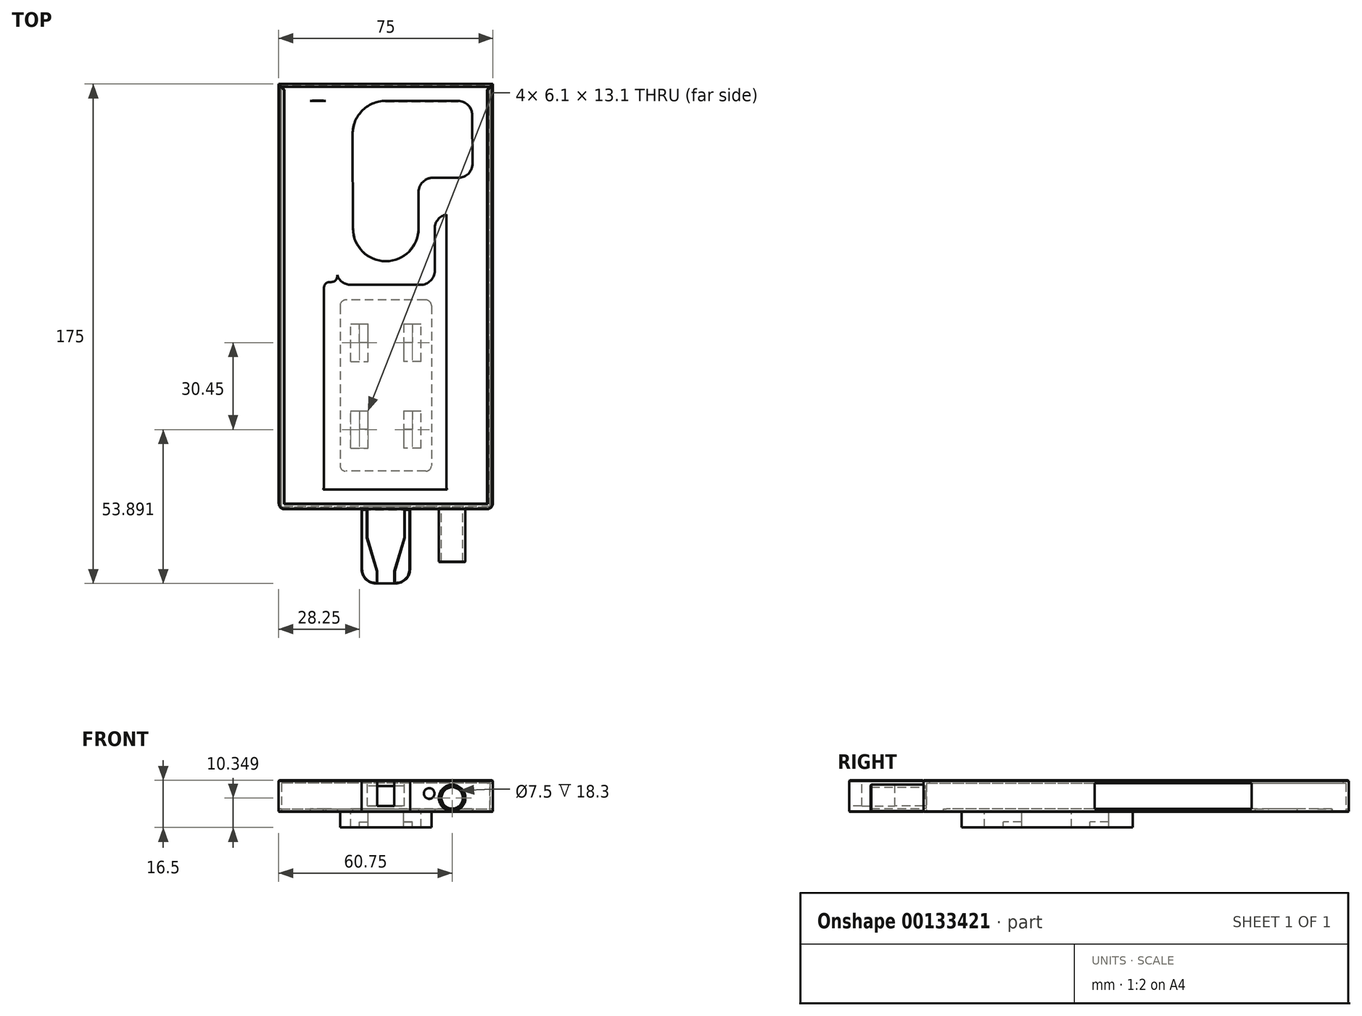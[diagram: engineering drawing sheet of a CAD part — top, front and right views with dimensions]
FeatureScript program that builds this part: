
annotation { "Feature Type Name" : "Feature", "Feature Type Description" : "" }
export const myFeature = defineFeature(function(context is Context, id is Id, definition is map)
    precondition{}
    {
        {
            var Q0;
            Q0=qCreatedBy(makeId("Top.planeOp"),FACE);
            var sketch = newSketch(context, id + "F0", { "sketchPlane" : qUnion([Q0])});
            skArc(sketch, "E0", {"start": v(-11.5, 23.98) * mm, "mid": v(-0.06, 12.4) * mm, "end": v(11.5, 23.87) * mm});
            skLineSegment(sketch, "E1", {"start": v(-11.5, 23.98) * mm, "end": v(-11.5, 23.99) * mm});
            skLineSegment(sketch, "E2", {"start": v(11.5, 23.99) * mm, "end": v(11.5, 23.87) * mm});
            skArc(sketch, "E3.MirrorCS", {"start": v(25.3, 68.56) * mm, "mid": v(28.83, 67.1) * mm, "end": v(30.3, 63.56) * mm});
            skLineSegment(sketch, "E4.MirrorCS", {"start": v(30.3, 63.56) * mm, "end": v(30.4, 46.61) * mm});
            skArc(sketch, "E5.MirrorCS", {"start": v(30.4, 46.61) * mm, "mid": v(28.94, 43.08) * mm, "end": v(25.4, 41.61) * mm});
            skArc(sketch, "E6.MirrorCS", {"start": v(-11.59, 56.36) * mm, "mid": v(-8.48, 64.94) * mm, "end": v(-0.11, 68.56) * mm});
            skArc(sketch, "E7.MirrorCS", {"start": v(11.5, 23.98) * mm, "mid": v(0.06, 12.4) * mm, "end": v(-11.5, 23.87) * mm});
            skLineSegment(sketch, "E8.MirrorCS", {"start": v(-0.11, 68.56) * mm, "end": v(25.3, 68.56) * mm});
            skLineSegment(sketch, "E9.MirrorCS", {"start": v(11.5, 41.61) * mm, "end": v(25.4, 41.61) * mm});
            skLineSegment(sketch, "E10.MirrorCS", {"start": v(-11.59, 56.36) * mm, "end": v(-11.5, 23.87) * mm});
            skLineSegment(sketch, "E11.MirrorCS", {"start": v(11.5, 23.98) * mm, "end": v(11.5, 41.61) * mm});
            skLineSegment(sketch, "E12.bottom", {"start": v(36.5, -73.5) * mm, "end": v(-36.5, -73.5) * mm});
            skLineSegment(sketch, "E12.top", {"start": v(36.5, 73.5) * mm, "end": v(-36.5, 73.5) * mm});
            skLineSegment(sketch, "E12.left", {"start": v(36.5, -73.5) * mm, "end": v(36.5, 73.5) * mm});
            skLineSegment(sketch, "E12.right", {"start": v(-36.5, -73.5) * mm, "end": v(-36.5, 73.5) * mm});
            skPoint(sketch, "E12.middle", {"position": v(0, 0) * mm});
            skLineSegment(sketch, "E13", {"start": v(-30.34, 33.69) * mm, "end": v(-30.34, -62.54) * mm});
            skLineSegment(sketch, "E14", {"start": v(-25.34, -67.54) * mm, "end": v(25, -67.54) * mm});
            skLineSegment(sketch, "E15", {"start": v(30, -62.54) * mm, "end": v(30, -50.72) * mm});
            skLineSegment(sketch, "E16", {"start": v(30, -50.72) * mm, "end": v(30, 23.85) * mm});
            skLineSegment(sketch, "E17", {"start": v(25, 28.85) * mm, "end": v(22.14, 28.85) * mm});
            skLineSegment(sketch, "E18", {"start": v(17.14, 23.85) * mm, "end": v(17.14, 9.12) * mm});
            skLineSegment(sketch, "E19", {"start": v(12.14, 4.12) * mm, "end": v(-9.2, 4.12) * mm});
            skLineSegment(sketch, "E20", {"start": v(-30.34, 33.69) * mm, "end": v(-30.34, 63.64) * mm});
            skLineSegment(sketch, "E21", {"start": v(-25.34, 68.64) * mm, "end": v(-22.26, 68.64) * mm});
            skLineSegment(sketch, "E22", {"start": v(-17.26, 63.64) * mm, "end": v(-17.26, 15.4) * mm});
            skLineSegment(sketch, "E23", {"start": v(-17.26, 15.4) * mm, "end": v(-17.26, 9.12) * mm});
            skLineSegment(sketch, "E24", {"start": v(-12.26, 4.12) * mm, "end": v(-9.2, 4.12) * mm});
            skPoint(sketch, "E25.visualSharp", {"position": v(17.14, 28.85) * mm});
            skArc(sketch, "E25.filletArc", {"start": v(22.14, 28.85) * mm, "mid": v(18.6, 27.39) * mm, "end": v(17.14, 23.85) * mm});
            skPoint(sketch, "E26.visualSharp", {"position": v(30, 28.85) * mm});
            skArc(sketch, "E26.filletArc", {"start": v(30, 23.85) * mm, "mid": v(28.54, 27.39) * mm, "end": v(25, 28.85) * mm});
            skPoint(sketch, "E27.visualSharp", {"position": v(17.14, 4.12) * mm});
            skArc(sketch, "E27.filletArc", {"start": v(12.14, 4.12) * mm, "mid": v(15.68, 5.59) * mm, "end": v(17.14, 9.12) * mm});
            skPoint(sketch, "E28.visualSharp", {"position": v(-17.26, 4.12) * mm});
            skArc(sketch, "E28.filletArc", {"start": v(-17.26, 9.12) * mm, "mid": v(-15.8, 5.59) * mm, "end": v(-12.26, 4.12) * mm});
            skPoint(sketch, "E29.visualSharp", {"position": v(-17.26, 68.64) * mm});
            skArc(sketch, "E29.filletArc", {"start": v(-17.26, 63.64) * mm, "mid": v(-18.72, 67.17) * mm, "end": v(-22.26, 68.64) * mm});
            skPoint(sketch, "E30.visualSharp", {"position": v(-30.34, -67.54) * mm});
            skArc(sketch, "E30.filletArc", {"start": v(-30.34, -62.54) * mm, "mid": v(-28.87, -66.07) * mm, "end": v(-25.34, -67.54) * mm});
            skPoint(sketch, "E31.visualSharp", {"position": v(30, -67.54) * mm});
            skArc(sketch, "E31.filletArc", {"start": v(25, -67.54) * mm, "mid": v(28.54, -66.07) * mm, "end": v(30, -62.54) * mm});
            skPoint(sketch, "E32.visualSharp", {"position": v(-30.34, 68.64) * mm});
            skArc(sketch, "E32.filletArc", {"start": v(-25.34, 68.64) * mm, "mid": v(-28.87, 67.17) * mm, "end": v(-30.34, 63.64) * mm});
            skLineSegment(sketch, "E33.0", {"start": v(37.5, 74.5) * mm, "end": v(-37.5, 74.5) * mm});
            skLineSegment(sketch, "E33.1", {"start": v(37.5, -74.5) * mm, "end": v(37.5, 74.5) * mm});
            skLineSegment(sketch, "E33.2", {"start": v(37.5, -74.5) * mm, "end": v(-37.5, -74.5) * mm});
            skLineSegment(sketch, "E33.3", {"start": v(-37.5, -74.5) * mm, "end": v(-37.5, 74.5) * mm});
            skSolve(sketch);
        }
        {
            var Q0;
            Q0=makeQuery(id+"F0.imprint","IMPRINT",FACE,{"disambiguationData":[TD([[makeQuery(id+"F0.imprint","IMPRINT",EDGE,{"derivedFrom":sQuery(id+"F0.wireOp",EDGE,"E13")}),1.0]])]});
            var Q1;
            Q1=makeQuery(id+"F0.imprint","IMPRINT",FACE,{"disambiguationData":[TD([[makeQuery(id+"F0.imprint","IMPRINT",EDGE,{"derivedFrom":sQuery(id+"F0.wireOp",EDGE,"E3.MirrorCS")}),1.0]])]});
            extrude(context, id + "F1", {"entities" : qUnion([Q0, Q1]), "depth" : 1 * mm});
        }
        {
            var Q0;
            Q0=makeQuery(id+"F1.opExtrude","CAP_FACE",FACE,{"disambiguationData":[OSD([sQuery(id+"F0.wireOp",EDGE,"E3.MirrorCS"),sQuery(id+"F0.wireOp",EDGE,"E4.MirrorCS"),sQuery(id+"F0.wireOp",EDGE,"E5.MirrorCS"),sQuery(id+"F0.wireOp",EDGE,"E6.MirrorCS"),sQuery(id+"F0.wireOp",EDGE,"E7.MirrorCS"),sQuery(id+"F0.wireOp",EDGE,"E8.MirrorCS"),sQuery(id+"F0.wireOp",EDGE,"E9.MirrorCS"),sQuery(id+"F0.wireOp",EDGE,"E10.MirrorCS"),sQuery(id+"F0.wireOp",EDGE,"E11.MirrorCS"),sQuery(id+"F0.wireOp",EDGE,"E12.bottom"),sQuery(id+"F0.wireOp",EDGE,"E12.top"),sQuery(id+"F0.wireOp",EDGE,"E12.left"),sQuery(id+"F0.wireOp",EDGE,"E12.right")])],"isStart":true});
            var sketch = newSketch(context, id + "F2", { "sketchPlane" : qUnion([Q0])});
            skLineSegment(sketch, "E34.bottom", {"start": v(14, 1.16) * mm, "end": v(-14, 1.16) * mm});
            skLineSegment(sketch, "E34.top", {"start": v(14, 61.16) * mm, "end": v(-14, 61.16) * mm});
            skLineSegment(sketch, "E34.left", {"start": v(16, 3.16) * mm, "end": v(16, 59.16) * mm});
            skLineSegment(sketch, "E34.right", {"start": v(-16, 3.16) * mm, "end": v(-16, 59.16) * mm});
            skPoint(sketch, "E34.middle", {"position": v(0, 31.16) * mm});
            skPoint(sketch, "E35.visualSharp", {"position": v(-16, 61.16) * mm});
            skArc(sketch, "E35.filletArc", {"start": v(-14, 61.16) * mm, "mid": v(-15.41, 60.57) * mm, "end": v(-16, 59.16) * mm});
            skPoint(sketch, "E36.visualSharp", {"position": v(16, 61.16) * mm});
            skArc(sketch, "E36.filletArc", {"start": v(16, 59.16) * mm, "mid": v(15.41, 60.57) * mm, "end": v(14, 61.16) * mm});
            skPoint(sketch, "E37.visualSharp", {"position": v(-16, 1.16) * mm});
            skArc(sketch, "E37.filletArc", {"start": v(-16, 3.16) * mm, "mid": v(-15.41, 1.75) * mm, "end": v(-14, 1.16) * mm});
            skPoint(sketch, "E38.visualSharp", {"position": v(16, 1.16) * mm});
            skArc(sketch, "E38.filletArc", {"start": v(14, 1.16) * mm, "mid": v(15.41, 1.75) * mm, "end": v(16, 3.16) * mm});
            skLineSegment(sketch, "E39.bottom", {"start": v(-12.3, 53.16) * mm, "end": v(-6.2, 53.16) * mm});
            skLineSegment(sketch, "E39.top", {"start": v(-12.3, 40.06) * mm, "end": v(-6.2, 40.06) * mm});
            skLineSegment(sketch, "E39.left", {"start": v(-12.3, 53.16) * mm, "end": v(-12.3, 40.06) * mm});
            skLineSegment(sketch, "E39.right", {"start": v(-6.2, 53.16) * mm, "end": v(-6.2, 40.06) * mm});
            skPoint(sketch, "E40.oppositeSnap0", {"position": v(-9.25, 40.06) * mm});
            skLineSegment(sketch, "E40.bottom", {"start": v(-6.2, 40.06) * mm, "end": v(-9.25, 40.06) * mm});
            skLineSegment(sketch, "E40.top", {"start": v(-6.2, 46.56) * mm, "end": v(-9.25, 46.56) * mm});
            skLineSegment(sketch, "E40.left", {"start": v(-6.2, 40.06) * mm, "end": v(-6.2, 46.56) * mm});
            skLineSegment(sketch, "E40.right", {"start": v(-9.25, 40.06) * mm, "end": v(-9.25, 46.56) * mm});
            skLineSegment(sketch, "E41.MirrorCS", {"start": v(6.2, 40.06) * mm, "end": v(6.2, 46.56) * mm});
            skLineSegment(sketch, "E42.MirrorCS", {"start": v(6.2, 46.56) * mm, "end": v(9.25, 46.56) * mm});
            skPoint(sketch, "E43.MirrorP", {"position": v(9.25, 40.06) * mm});
            skLineSegment(sketch, "E44.MirrorCS", {"start": v(9.25, 40.06) * mm, "end": v(9.25, 46.56) * mm});
            skLineSegment(sketch, "E45.MirrorCS", {"start": v(6.2, 53.16) * mm, "end": v(6.2, 40.06) * mm});
            skLineSegment(sketch, "E46.MirrorCS", {"start": v(6.2, 40.06) * mm, "end": v(9.25, 40.06) * mm});
            skLineSegment(sketch, "E47.MirrorCS", {"start": v(12.3, 53.16) * mm, "end": v(12.3, 40.06) * mm});
            skLineSegment(sketch, "E48.MirrorCS", {"start": v(12.3, 40.06) * mm, "end": v(6.2, 40.06) * mm});
            skLineSegment(sketch, "E49.MirrorCS", {"start": v(12.3, 53.16) * mm, "end": v(6.2, 53.16) * mm});
            skLineSegment(sketch, "E50", {"start": v(-16, 31.16) * mm, "end": v(16, 31.16) * mm, "construction": true});
            skLineSegment(sketch, "E51.bottom", {"start": v(-12.3, 22.7) * mm, "end": v(-6.2, 22.7) * mm});
            skLineSegment(sketch, "E51.top", {"start": v(-12.3, 9.6) * mm, "end": v(-6.2, 9.6) * mm});
            skLineSegment(sketch, "E51.left", {"start": v(-12.3, 22.7) * mm, "end": v(-12.3, 9.6) * mm});
            skLineSegment(sketch, "E51.right", {"start": v(-6.2, 22.7) * mm, "end": v(-6.2, 9.6) * mm});
            skPoint(sketch, "E52.oppositeSnap0", {"position": v(-9.25, 9.6) * mm});
            skLineSegment(sketch, "E52.bottom", {"start": v(-6.2, 9.6) * mm, "end": v(-9.25, 9.6) * mm});
            skLineSegment(sketch, "E52.top", {"start": v(-6.2, 16.1) * mm, "end": v(-9.25, 16.1) * mm});
            skLineSegment(sketch, "E52.left", {"start": v(-6.2, 9.6) * mm, "end": v(-6.2, 16.1) * mm});
            skLineSegment(sketch, "E52.right", {"start": v(-9.25, 9.6) * mm, "end": v(-9.25, 16.1) * mm});
            skLineSegment(sketch, "E53.MirrorCS", {"start": v(6.2, 9.6) * mm, "end": v(6.2, 16.1) * mm});
            skLineSegment(sketch, "E54.MirrorCS", {"start": v(6.2, 16.1) * mm, "end": v(9.27, 16.1) * mm});
            skPoint(sketch, "E55.MirrorP", {"position": v(9.52, 10.68) * mm});
            skLineSegment(sketch, "E56.MirrorCS", {"start": v(9.25, 9.6) * mm, "end": v(9.27, 16.1) * mm});
            skLineSegment(sketch, "E57.MirrorCS", {"start": v(6.2, 22.7) * mm, "end": v(6.2, 9.6) * mm});
            skLineSegment(sketch, "E58.MirrorCS", {"start": v(6.2, 9.6) * mm, "end": v(9.25, 9.6) * mm});
            skLineSegment(sketch, "E59.MirrorCS", {"start": v(12.3, 22.7) * mm, "end": v(12.3, 9.6) * mm});
            skLineSegment(sketch, "E60.MirrorCS", {"start": v(12.3, 9.6) * mm, "end": v(6.2, 9.6) * mm});
            skLineSegment(sketch, "E61.MirrorCS", {"start": v(12.3, 22.7) * mm, "end": v(6.2, 22.7) * mm});
            skSolve(sketch);
        }
        {
            var Q0;
            Q0=makeQuery(id+"F2.imprint","IMPRINT",FACE,{"disambiguationData":[TD([[makeQuery(id+"F2.imprint","IMPRINT",EDGE,{"derivedFrom":sQuery(id+"F2.wireOp",EDGE,"E34.bottom")}),-1.0]])]});
            extrude(context, id + "F3", {"entities" : qUnion([Q0]), "depth" : 3.5 * mm});
        }
        {
            var Q0;
            Q0=makeQuery(id+"F3.opExtrude","CAP_FACE",FACE,{"disambiguationData":[OSD([sQuery(id+"F2.wireOp",EDGE,"E34.bottom"),sQuery(id+"F2.wireOp",EDGE,"E34.top"),sQuery(id+"F2.wireOp",EDGE,"E34.left"),sQuery(id+"F2.wireOp",EDGE,"E34.right"),sQuery(id+"F2.wireOp",EDGE,"E35.filletArc"),sQuery(id+"F2.wireOp",EDGE,"E36.filletArc"),sQuery(id+"F2.wireOp",EDGE,"E37.filletArc"),sQuery(id+"F2.wireOp",EDGE,"E38.filletArc"),sQuery(id+"F2.wireOp",EDGE,"E39.bottom"),sQuery(id+"F2.wireOp",EDGE,"E39.top"),sQuery(id+"F2.wireOp",EDGE,"E39.left"),sQuery(id+"F2.wireOp",EDGE,"E39.right"),sQuery(id+"F2.wireOp",EDGE,"E40.bottom"),sQuery(id+"F2.wireOp",EDGE,"E40.left"),sQuery(id+"F2.wireOp",EDGE,"E45.MirrorCS"),sQuery(id+"F2.wireOp",EDGE,"E47.MirrorCS"),sQuery(id+"F2.wireOp",EDGE,"E48.MirrorCS"),sQuery(id+"F2.wireOp",EDGE,"E49.MirrorCS"),sQuery(id+"F2.wireOp",EDGE,"E51.bottom"),sQuery(id+"F2.wireOp",EDGE,"E51.top"),sQuery(id+"F2.wireOp",EDGE,"E51.left"),sQuery(id+"F2.wireOp",EDGE,"E51.right"),sQuery(id+"F2.wireOp",EDGE,"E52.bottom"),sQuery(id+"F2.wireOp",EDGE,"E52.left"),sQuery(id+"F2.wireOp",EDGE,"E53.MirrorCS"),sQuery(id+"F2.wireOp",EDGE,"E54.MirrorCS"),sQuery(id+"F2.wireOp",EDGE,"E57.MirrorCS"),sQuery(id+"F2.wireOp",EDGE,"E59.MirrorCS"),sQuery(id+"F2.wireOp",EDGE,"E60.MirrorCS"),sQuery(id+"F2.wireOp",EDGE,"E61.MirrorCS")])],"isStart":false});
            var sketch = newSketch(context, id + "F4", { "sketchPlane" : qUnion([Q0])});
            skLineSegment(sketch, "E62.0", {"start": v(-6.2, 46.56) * mm, "end": v(-9.25, 46.56) * mm});
            skLineSegment(sketch, "E63.0", {"start": v(-9.25, 40.06) * mm, "end": v(-9.25, 46.56) * mm});
            skLineSegment(sketch, "E64.0.0", {"start": v(9.25, 46.56) * mm, "end": v(6.2, 46.56) * mm});
            skLineSegment(sketch, "E64.0.3", {"start": v(9.25, 40.06) * mm, "end": v(9.25, 46.56) * mm});
            skLineSegment(sketch, "E65.0.3", {"start": v(-9.25, 46.56) * mm, "end": v(-9.25, 40.06) * mm});
            skLineSegment(sketch, "E66.0.2", {"start": v(-6.2, 16.1) * mm, "end": v(-9.25, 16.1) * mm});
            skLineSegment(sketch, "E66.0.3", {"start": v(-9.25, 16.1) * mm, "end": v(-9.25, 9.6) * mm});
            skLineSegment(sketch, "E67.0.0", {"start": v(9.27, 16.1) * mm, "end": v(6.2, 16.1) * mm});
            skLineSegment(sketch, "E67.0.3", {"start": v(9.25, 9.6) * mm, "end": v(9.27, 16.1) * mm});
            skLineSegment(sketch, "E68.0.0", {"start": v(-14, 1.16) * mm, "end": v(14, 1.16) * mm});
            skArc(sketch, "E68.0.1", {"start": v(14, 1.16) * mm, "mid": v(15.41, 1.75) * mm, "end": v(16, 3.16) * mm});
            skLineSegment(sketch, "E68.0.2", {"start": v(16, 3.16) * mm, "end": v(16, 59.16) * mm});
            skArc(sketch, "E68.0.3", {"start": v(16, 59.16) * mm, "mid": v(15.41, 60.57) * mm, "end": v(14, 61.16) * mm});
            skLineSegment(sketch, "E68.0.4", {"start": v(14, 61.16) * mm, "end": v(-14, 61.16) * mm});
            skArc(sketch, "E68.0.5", {"start": v(-14, 61.16) * mm, "mid": v(-15.41, 60.57) * mm, "end": v(-16, 59.16) * mm});
            skLineSegment(sketch, "E68.0.6", {"start": v(-16, 59.16) * mm, "end": v(-16, 3.16) * mm});
            skArc(sketch, "E68.0.7", {"start": v(-16, 3.16) * mm, "mid": v(-15.41, 1.75) * mm, "end": v(-14, 1.16) * mm});
            skLineSegment(sketch, "E69.0.0", {"start": v(-6.2, 53.16) * mm, "end": v(-12.3, 53.16) * mm});
            skLineSegment(sketch, "E69.0.1", {"start": v(-12.3, 53.16) * mm, "end": v(-12.3, 40.06) * mm});
            skLineSegment(sketch, "E69.0.2", {"start": v(-12.3, 40.06) * mm, "end": v(-9.25, 40.06) * mm});
            skLineSegment(sketch, "E69.0.4", {"start": v(-9.25, 46.56) * mm, "end": v(-6.2, 46.56) * mm});
            skLineSegment(sketch, "E69.0.5", {"start": v(-6.2, 46.56) * mm, "end": v(-6.2, 53.16) * mm});
            skLineSegment(sketch, "E70.0.0", {"start": v(6.2, 53.16) * mm, "end": v(6.2, 46.56) * mm});
            skLineSegment(sketch, "E70.0.1", {"start": v(6.2, 46.56) * mm, "end": v(9.25, 46.56) * mm});
            skLineSegment(sketch, "E70.0.2", {"start": v(9.25, 46.56) * mm, "end": v(9.25, 40.06) * mm});
            skLineSegment(sketch, "E70.0.3", {"start": v(9.25, 40.06) * mm, "end": v(12.3, 40.06) * mm});
            skLineSegment(sketch, "E70.0.4", {"start": v(12.3, 40.06) * mm, "end": v(12.3, 53.16) * mm});
            skLineSegment(sketch, "E70.0.5", {"start": v(12.3, 53.16) * mm, "end": v(6.2, 53.16) * mm});
            skLineSegment(sketch, "E71.0.0", {"start": v(6.2, 22.7) * mm, "end": v(6.2, 16.1) * mm});
            skLineSegment(sketch, "E71.0.1", {"start": v(6.2, 16.1) * mm, "end": v(9.27, 16.1) * mm});
            skLineSegment(sketch, "E71.0.2", {"start": v(9.27, 16.1) * mm, "end": v(9.25, 9.6) * mm});
            skLineSegment(sketch, "E71.0.3", {"start": v(9.25, 9.6) * mm, "end": v(12.3, 9.6) * mm});
            skLineSegment(sketch, "E71.0.4", {"start": v(12.3, 9.6) * mm, "end": v(12.3, 22.7) * mm});
            skLineSegment(sketch, "E71.0.5", {"start": v(12.3, 22.7) * mm, "end": v(6.2, 22.7) * mm});
            skLineSegment(sketch, "E72.0.0", {"start": v(-6.2, 22.7) * mm, "end": v(-12.3, 22.7) * mm});
            skLineSegment(sketch, "E72.0.1", {"start": v(-12.3, 22.7) * mm, "end": v(-12.3, 9.6) * mm});
            skLineSegment(sketch, "E72.0.2", {"start": v(-12.3, 9.6) * mm, "end": v(-9.25, 9.6) * mm});
            skLineSegment(sketch, "E72.0.3", {"start": v(-9.25, 9.6) * mm, "end": v(-9.25, 16.1) * mm});
            skLineSegment(sketch, "E72.0.4", {"start": v(-9.25, 16.1) * mm, "end": v(-6.2, 16.1) * mm});
            skLineSegment(sketch, "E72.0.5", {"start": v(-6.2, 16.1) * mm, "end": v(-6.2, 22.7) * mm});
            skSolve(sketch);
        }
        {
            var Q0;
            Q0 = qSketchRegion(id + "F4", true);
            extrude(context, id + "F5", {"entities" : qUnion([Q0]), "operationType" : NewBodyOperationType.ADD, "depth" : 2 * mm});
        }
        {
            var Q0;
            Q0=makeQuery(id+"F1.opExtrude","CAP_FACE",FACE,{"disambiguationData":[OSD([sQuery(id+"F0.wireOp",EDGE,"E3.MirrorCS"),sQuery(id+"F0.wireOp",EDGE,"E4.MirrorCS"),sQuery(id+"F0.wireOp",EDGE,"E5.MirrorCS"),sQuery(id+"F0.wireOp",EDGE,"E6.MirrorCS"),sQuery(id+"F0.wireOp",EDGE,"E7.MirrorCS"),sQuery(id+"F0.wireOp",EDGE,"E8.MirrorCS"),sQuery(id+"F0.wireOp",EDGE,"E9.MirrorCS"),sQuery(id+"F0.wireOp",EDGE,"E10.MirrorCS"),sQuery(id+"F0.wireOp",EDGE,"E11.MirrorCS"),sQuery(id+"F0.wireOp",EDGE,"E12.bottom"),sQuery(id+"F0.wireOp",EDGE,"E12.top"),sQuery(id+"F0.wireOp",EDGE,"E12.left"),sQuery(id+"F0.wireOp",EDGE,"E12.right")])],"isStart":false});
            var sketch = newSketch(context, id + "F6", { "sketchPlane" : qUnion([Q0])});
            skLineSegment(sketch, "E73.0", {"start": v(-19.04, 68.5) * mm, "end": v(-29.5, 68.5) * mm});
            skLineSegment(sketch, "E73.1", {"start": v(31.5, -66.5) * mm, "end": v(31.5, 33.24) * mm});
            skLineSegment(sketch, "E73.2", {"start": v(29.5, -68.5) * mm, "end": v(23.21, -68.5) * mm});
            skLineSegment(sketch, "E73.3", {"start": v(-31.5, -66.5) * mm, "end": v(-31.5, 66.5) * mm});
            skLineSegment(sketch, "E74", {"start": v(-17.04, 66.5) * mm, "end": v(-17.04, 7.11) * mm});
            skLineSegment(sketch, "E75", {"start": v(21.21, 5.11) * mm, "end": v(21.21, -66.5) * mm});
            skLineSegment(sketch, "E76", {"start": v(-19.04, 5.11) * mm, "end": v(-19.65, 5.11) * mm});
            skLineSegment(sketch, "E77", {"start": v(-21.65, 3.11) * mm, "end": v(-21.65, -66.5) * mm});
            skLineSegment(sketch, "E78", {"start": v(21.21, 5.11) * mm, "end": v(21.21, 33.24) * mm});
            skLineSegment(sketch, "E79", {"start": v(23.21, 35.24) * mm, "end": v(29.5, 35.24) * mm});
            skPoint(sketch, "E80.visualSharp", {"position": v(-21.65, 5.11) * mm});
            skArc(sketch, "E80.filletArc", {"start": v(-19.65, 5.11) * mm, "mid": v(-21.07, 4.52) * mm, "end": v(-21.65, 3.11) * mm});
            skPoint(sketch, "E81.visualSharp", {"position": v(-17.04, 5.11) * mm});
            skArc(sketch, "E81.filletArc", {"start": v(-19.04, 5.11) * mm, "mid": v(-17.62, 5.7) * mm, "end": v(-17.04, 7.11) * mm});
            skPoint(sketch, "E82.visualSharp", {"position": v(21.21, 35.24) * mm});
            skArc(sketch, "E82.filletArc", {"start": v(23.21, 35.24) * mm, "mid": v(21.8, 34.65) * mm, "end": v(21.21, 33.24) * mm});
            skPoint(sketch, "E83.visualSharp", {"position": v(-31.5, 68.5) * mm});
            skArc(sketch, "E83.filletArc", {"start": v(-29.5, 68.5) * mm, "mid": v(-30.91, 67.91) * mm, "end": v(-31.5, 66.5) * mm});
            skPoint(sketch, "E84.visualSharp", {"position": v(-31.5, -68.5) * mm});
            skArc(sketch, "E84.filletArc", {"start": v(-31.5, -66.5) * mm, "mid": v(-30.91, -67.91) * mm, "end": v(-29.5, -68.5) * mm});
            skPoint(sketch, "E85.visualSharp", {"position": v(31.5, -68.5) * mm});
            skArc(sketch, "E85.filletArc", {"start": v(29.5, -68.5) * mm, "mid": v(30.91, -67.91) * mm, "end": v(31.5, -66.5) * mm});
            skArc(sketch, "E86.filletArc", {"start": v(21.21, -66.5) * mm, "mid": v(21.8, -67.91) * mm, "end": v(23.21, -68.5) * mm});
            skLineSegment(sketch, "E87", {"start": v(-29.5, -68.5) * mm, "end": v(-23.65, -68.5) * mm});
            skPoint(sketch, "E88.visualSharp", {"position": v(-21.65, -68.5) * mm});
            skArc(sketch, "E88.filletArc", {"start": v(-23.65, -68.5) * mm, "mid": v(-22.24, -67.91) * mm, "end": v(-21.65, -66.5) * mm});
            skPoint(sketch, "E89.visualSharp", {"position": v(31.5, 35.24) * mm});
            skArc(sketch, "E89.filletArc", {"start": v(31.5, 33.24) * mm, "mid": v(30.91, 34.65) * mm, "end": v(29.5, 35.24) * mm});
            skPoint(sketch, "E90.visualSharp", {"position": v(-17.04, 68.5) * mm});
            skArc(sketch, "E90.filletArc", {"start": v(-17.04, 66.5) * mm, "mid": v(-17.62, 67.91) * mm, "end": v(-19.04, 68.5) * mm});
            skSolve(sketch);
        }
        {
            var Q0;
            {var subQ1=sQuery(id+"F6.wireOp",EDGE,"E73.3");Q0=makeQuery(id+"F6.imprint","IMPRINT",FACE,{"disambiguationData":[TD([[makeQuery(id+"F6.imprint","IMPRINT",EDGE,{"derivedFrom":subQ1}),-1.0]])]});}
            var Q1;
            {var subQ3=sQuery(id+"F6.wireOp",EDGE,"E75");Q1=makeQuery(id+"F6.imprint","IMPRINT",FACE,{"disambiguationData":[TD([[makeQuery(id+"F6.imprint","IMPRINT",EDGE,{"derivedFrom":subQ3}),1.0]])]});}
            extrude(context, id + "F7", {"entities" : qUnion([Q0, Q1]), "operationType" : NewBodyOperationType.REMOVE, "oppositeDirection" : true, "depth" : 1 * mm});
        }
        {
            var Q0;
            Q0=makeQuery(id+"F0.imprint","IMPRINT",FACE,{"disambiguationData":[TD([[makeQuery(id+"F0.imprint","IMPRINT",EDGE,{"derivedFrom":sQuery(id+"F0.wireOp",EDGE,"E12.bottom")}),1.0]])]});
            extrude(context, id + "F8", {"entities" : qUnion([Q0]), "operationType" : NewBodyOperationType.ADD, "depth" : 10 * mm});
        }
        {
            var Q0;
            Q0=makeQuery(id+"F8.opExtrude","CAP_FACE",FACE,{"disambiguationData":[OSD([sQuery(id+"F0.wireOp",EDGE,"E12.bottom"),sQuery(id+"F0.wireOp",EDGE,"E12.top"),sQuery(id+"F0.wireOp",EDGE,"E12.left"),sQuery(id+"F0.wireOp",EDGE,"E12.right"),sQuery(id+"F0.wireOp",EDGE,"E33.0"),sQuery(id+"F0.wireOp",EDGE,"E33.1"),sQuery(id+"F0.wireOp",EDGE,"E33.2"),sQuery(id+"F0.wireOp",EDGE,"E33.3")])],"isStart":false});
            var sketch = newSketch(context, id + "F9", { "sketchPlane" : qUnion([Q0])});
            skLineSegment(sketch, "E91", {"start": v(-37.5, 74.5) * mm, "end": v(-36.5, 73.5) * mm});
            skLineSegment(sketch, "E92", {"start": v(36.5, 73.5) * mm, "end": v(37.5, 74.5) * mm});
            skLineSegment(sketch, "E93", {"start": v(36.5, 40.5) * mm, "end": v(37.5, 40.5) * mm});
            skLineSegment(sketch, "E94", {"start": v(36.5, -14.5) * mm, "end": v(37.5, -14.5) * mm});
            skLineSegment(sketch, "E95.0", {"start": v(35.5, 72.5) * mm, "end": v(-35.5, 72.5) * mm});
            skLineSegment(sketch, "E95.1", {"start": v(35.5, -72.5) * mm, "end": v(35.5, 72.5) * mm});
            skLineSegment(sketch, "E95.2", {"start": v(35.5, -72.5) * mm, "end": v(-35.5, -72.5) * mm});
            skLineSegment(sketch, "E95.3", {"start": v(-35.5, -72.5) * mm, "end": v(-35.5, 72.5) * mm});
            skLineSegment(sketch, "E96", {"start": v(36.5, 40.5) * mm, "end": v(35.5, 40.5) * mm});
            skLineSegment(sketch, "E97", {"start": v(36.5, -14.5) * mm, "end": v(35.5, -14.5) * mm});
            skLineSegment(sketch, "E98", {"start": v(-35.5, 72.5) * mm, "end": v(-36.5, 73.5) * mm});
            skLineSegment(sketch, "E99", {"start": v(35.5, 72.5) * mm, "end": v(36.5, 73.5) * mm});
            skSolve(sketch);
        }
        {
            var Q0;
            Q0=makeQuery(id+"F9.imprint","IMPRINT",FACE,{"disambiguationData":[TD([[makeQuery(id+"F9.imprint","IMPRINT",EDGE,{"derivedFrom":sQuery(id+"F9.wireOp",EDGE,"E91")}),1.0]])]});
            var Q1;
            {var subQ0=sQuery(id+"F9.wireOp",EDGE,"E93");Q1=makeQuery(id+"F9.imprint","IMPRINT",FACE,{"disambiguationData":[TD([[makeQuery(id+"F9.imprint","IMPRINT",EDGE,{"derivedFrom":subQ0}),-1.0]])]});}
            var Q2;
            Q2=makeQuery(id+"F1.opExtrude","CAP_FACE",FACE,{"disambiguationData":[OSD([sQuery(id+"F0.wireOp",EDGE,"E3.MirrorCS"),sQuery(id+"F0.wireOp",EDGE,"E4.MirrorCS"),sQuery(id+"F0.wireOp",EDGE,"E5.MirrorCS"),sQuery(id+"F0.wireOp",EDGE,"E6.MirrorCS"),sQuery(id+"F0.wireOp",EDGE,"E7.MirrorCS"),sQuery(id+"F0.wireOp",EDGE,"E8.MirrorCS"),sQuery(id+"F0.wireOp",EDGE,"E9.MirrorCS"),sQuery(id+"F0.wireOp",EDGE,"E10.MirrorCS"),sQuery(id+"F0.wireOp",EDGE,"E11.MirrorCS"),sQuery(id+"F0.wireOp",EDGE,"E12.bottom"),sQuery(id+"F0.wireOp",EDGE,"E12.top"),sQuery(id+"F0.wireOp",EDGE,"E12.left"),sQuery(id+"F0.wireOp",EDGE,"E12.right")])],"isStart":false});
            extrude(context, id + "F10", {"entities" : qUnion([Q0, Q1]), "operationType" : NewBodyOperationType.REMOVE, "endBound" : BoundingType.UP_TO_SURFACE, "oppositeDirection" : true, "endBoundEntityFace" : qUnion([Q2]), "depth" : 25 * mm});
        }
        {
            var Q0;
            {var subQ2=sQuery(id+"F9.wireOp",EDGE,"E95.2");Q0=makeQuery(id+"F9.imprint","IMPRINT",FACE,{"disambiguationData":[TD([[makeQuery(id+"F9.imprint","IMPRINT",EDGE,{"derivedFrom":subQ2}),1.0]])]});}
            var Q1;
            Q1=makeQuery(id+"F9.imprint","IMPRINT",FACE,{"disambiguationData":[TD([[makeQuery(id+"F9.imprint","IMPRINT",EDGE,{"derivedFrom":sQuery(id+"F9.wireOp",EDGE,"E91")}),-1.0]])]});
            var Q2;
            {var subQ0=sQuery(id+"F9.wireOp",EDGE,"E92");Q2=makeQuery(id+"F9.imprint","IMPRINT",FACE,{"disambiguationData":[TD([[makeQuery(id+"F9.imprint","IMPRINT",EDGE,{"derivedFrom":subQ0}),-1.0]])]});}
            var Q3;
            {var subQ2=sQuery(id+"F9.wireOp",EDGE,"E96");Q3=makeQuery(id+"F9.imprint","IMPRINT",FACE,{"disambiguationData":[TD([[makeQuery(id+"F9.imprint","IMPRINT",EDGE,{"derivedFrom":subQ2}),-1.0]])]});}
            var Q4;
            {var subQ0=sQuery(id+"F9.wireOp",EDGE,"E93");Q4=makeQuery(id+"F9.imprint","IMPRINT",FACE,{"disambiguationData":[TD([[makeQuery(id+"F9.imprint","IMPRINT",EDGE,{"derivedFrom":subQ0}),-1.0]])]});}
            var Q5;
            {var subQ0=sQuery(id+"F9.wireOp",EDGE,"E96");Q5=makeQuery(id+"F9.imprint","IMPRINT",FACE,{"disambiguationData":[TD([[makeQuery(id+"F9.imprint","IMPRINT",EDGE,{"derivedFrom":subQ0}),1.0]])]});}
            extrude(context, id + "F11", {"entities" : qUnion([Q0, Q1, Q2, Q3, Q4, Q5]), "operationType" : NewBodyOperationType.ADD, "depth" : 1 * mm});
        }
        {
            var Q0;
            {var subQ0=sQuery(id+"F0.wireOp",EDGE,"E33.2");Q0=makeQuery(id+"F11.boolean.opBoolean","MERGE",FACE,{"derivedFrom":[makeQuery(id+"F8.opExtrude","SWEPT_FACE",FACE,{"disambiguationData":[OSD([subQ0])]}),makeQuery(id+"F11.opExtrude","SWEPT_FACE",FACE,{"disambiguationData":[OSD([subQ0])]})]});}
            var sketch = newSketch(context, id + "F12", { "sketchPlane" : qUnion([Q0])});
            skLineSegment(sketch, "E100.bottom", {"start": v(6.5, 2) * mm, "end": v(-6.5, 2) * mm});
            skLineSegment(sketch, "E100.top", {"start": v(6.5, 9) * mm, "end": v(-6.5, 9) * mm});
            skLineSegment(sketch, "E100.left", {"start": v(6.5, 2) * mm, "end": v(6.5, 9) * mm});
            skLineSegment(sketch, "E100.right", {"start": v(-6.5, 2) * mm, "end": v(-6.5, 9) * mm});
            skPoint(sketch, "E100.middle", {"position": v(0, 5.5) * mm});
            skPoint(sketch, "E100.middle.positionSnap0", {"position": v(-37.5, 5.5) * mm});
            skPoint(sketch, "E100.centerSnap0", {"position": v(-37.5, 5.5) * mm});
            skCircle(sketch, "E101", {"center": v(23.25, 4.85) * mm, "radius": 3.75 * mm});
            skCircle(sketch, "E102", {"center": v(15.2, 6.42) * mm, "radius": 1.87 * mm});
            skSolve(sketch);
        }
        {
            var Q0;
            Q0 = qSketchRegion(id + "F12", true);
            extrude(context, id + "F13", {"entities" : qUnion([Q0]), "operationType" : NewBodyOperationType.REMOVE, "endBound" : BoundingType.THROUGH_ALL, "oppositeDirection" : true, "depth" : 25 * mm});
        }
        {
            var Q0;
            {var subQ0=sQuery(id+"F0.wireOp",EDGE,"E33.2");var subQ1=sQuery(id+"F0.wireOp",EDGE,"E33.1");Q0=makeQuery(id+"F11.boolean.opBoolean","MERGE",EDGE,{"derivedFrom":[makeQuery(id+"F8.opExtrude","SWEPT_EDGE",EDGE,{"disambiguationData":[OSD([subQ1,subQ0])]}),makeQuery(id+"F11.opExtrude","SWEPT_EDGE",EDGE,{"disambiguationData":[OSD([subQ1,subQ0])]})]});}
            var Q1;
            {var subQ0=sQuery(id+"F0.wireOp",EDGE,"E33.3");var subQ1=sQuery(id+"F0.wireOp",EDGE,"E33.2");Q1=makeQuery(id+"F11.boolean.opBoolean","MERGE",EDGE,{"derivedFrom":[makeQuery(id+"F8.opExtrude","SWEPT_EDGE",EDGE,{"disambiguationData":[OSD([subQ1,subQ0])]}),makeQuery(id+"F11.opExtrude","SWEPT_EDGE",EDGE,{"disambiguationData":[OSD([subQ1,subQ0])]})]});}
            fillet(context, id + "F14", {"entities" : qUnion([Q0, Q1]), "radius" : 2 * mm, "tangentPropagation" : true, "allowEdgeOverflow" : false});
        }
        {
            var Q0;
            {var subQ0=sQuery(id+"F0.wireOp",EDGE,"E33.2");Q0=makeQuery(id+"F11.boolean.opBoolean","MERGE",FACE,{"derivedFrom":[makeQuery(id+"F8.opExtrude","SWEPT_FACE",FACE,{"disambiguationData":[OSD([subQ0])]}),makeQuery(id+"F11.opExtrude","SWEPT_FACE",FACE,{"disambiguationData":[OSD([subQ0])]})]});}
            var sketch = newSketch(context, id + "F15", { "sketchPlane" : qUnion([Q0])});
            skLineSegment(sketch, "E103.0", {"start": v(8.5, 11) * mm, "end": v(-8.5, 11) * mm});
            skLineSegment(sketch, "E103.1", {"start": v(8.5, 0) * mm, "end": v(8.5, 11) * mm});
            skLineSegment(sketch, "E103.2", {"start": v(8.5, 0) * mm, "end": v(-8.5, 0) * mm});
            skLineSegment(sketch, "E103.3", {"start": v(-8.5, 0) * mm, "end": v(-8.5, 11) * mm});
            skSolve(sketch);
        }
        {
            var Q0;
            Q0 = qSketchRegion(id + "F15", true);
            extrude(context, id + "F16", {"entities" : qUnion([Q0]), "depth" : 26 * mm});
        }
        {
            var Q0;
            Q0=makeQuery(id+"F16.opExtrude","CAP_FACE",FACE,{"disambiguationData":[OSD([sQuery(id+"F15.wireOp",EDGE,"E103.0"),sQuery(id+"F15.wireOp",EDGE,"E103.1"),sQuery(id+"F15.wireOp",EDGE,"E103.2"),sQuery(id+"F15.wireOp",EDGE,"E103.3")])],"isStart":false});
            var sketch = newSketch(context, id + "F17", { "sketchPlane" : qUnion([Q0])});
            skCircle(sketch, "E104", {"center": v(0, 5.5) * mm, "radius": 3 * mm});
            skPoint(sketch, "E104.centerSnap0", {"position": v(-8.5, 5.5) * mm});
            skSolve(sketch);
        }
        {
            var Q0;
            Q0 = qSketchRegion(id + "F17", true);
            var Q1;
            Q1=makeQuery(id+"F16.opExtrude","CAP_FACE",FACE,{"disambiguationData":[OSD([sQuery(id+"F15.wireOp",EDGE,"E103.0"),sQuery(id+"F15.wireOp",EDGE,"E103.1"),sQuery(id+"F15.wireOp",EDGE,"E103.2"),sQuery(id+"F15.wireOp",EDGE,"E103.3")])],"isStart":true});
            extrude(context, id + "F18", {"entities" : qUnion([Q0]), "operationType" : NewBodyOperationType.REMOVE, "endBound" : BoundingType.UP_TO_SURFACE, "oppositeDirection" : true, "endBoundEntityFace" : qUnion([Q1]), "depth" : 25 * mm});
        }
        {
            var Q0;
            Q0=makeQuery(id+"F16.opExtrude","SWEPT_FACE",FACE,{"disambiguationData":[OSD([sQuery(id+"F15.wireOp",EDGE,"E103.0")])]});
            var sketch = newSketch(context, id + "F19", { "sketchPlane" : qUnion([Q0])});
            skLineSegment(sketch, "E105.top", {"start": v(6.5, -74.5) * mm, "end": v(-6.5, -74.5) * mm});
            skLineSegment(sketch, "E105.left", {"start": v(6.5, -84.5) * mm, "end": v(6.5, -74.5) * mm});
            skLineSegment(sketch, "E105.right", {"start": v(-6.5, -84.5) * mm, "end": v(-6.5, -74.5) * mm});
            skPoint(sketch, "E105.middle", {"position": v(0, -79.5) * mm});
            skPoint(sketch, "E105.middle.positionSnap0", {"position": v(0, -100.5) * mm});
            skPoint(sketch, "E105.centerSnap0", {"position": v(0, -100.5) * mm});
            skLineSegment(sketch, "E106.0", {"start": v(3, -100.5) * mm, "end": v(-3, -100.5) * mm});
            skLineSegment(sketch, "E107", {"start": v(-3, -100.5) * mm, "end": v(-3, -96.1) * mm});
            skLineSegment(sketch, "E108", {"start": v(3, -96.1) * mm, "end": v(3, -100.5) * mm});
            skLineSegment(sketch, "E109", {"start": v(-6.5, -84.5) * mm, "end": v(-3, -96.1) * mm});
            skLineSegment(sketch, "E110", {"start": v(3, -96.1) * mm, "end": v(6.5, -84.5) * mm});
            skSolve(sketch);
        }
        {
            var Q0;
            Q0 = qSketchRegion(id + "F19", true);
            var Q1;
            Q1=makeQuery(id+"F13.boolean.opBoolean","COPY",FACE,{"derivedFrom":makeQuery(id+"F13.opExtrude","SWEPT_FACE",FACE,{"disambiguationData":[OSD([sQuery(id+"F12.wireOp",EDGE,"E100.bottom")])]})});
            extrude(context, id + "F20", {"entities" : qUnion([Q0]), "operationType" : NewBodyOperationType.REMOVE, "endBound" : BoundingType.UP_TO_SURFACE, "oppositeDirection" : true, "endBoundEntityFace" : qUnion([Q1]), "depth" : 8.6 * mm});
        }
        {
            var Q0;
            {var subQ0=sQuery(id+"F0.wireOp",EDGE,"E33.2");Q0=makeQuery(id+"F11.boolean.opBoolean","MERGE",FACE,{"derivedFrom":[makeQuery(id+"F8.opExtrude","SWEPT_FACE",FACE,{"disambiguationData":[OSD([subQ0])]}),makeQuery(id+"F11.opExtrude","SWEPT_FACE",FACE,{"disambiguationData":[OSD([subQ0])]})]});}
            var sketch = newSketch(context, id + "F21", { "sketchPlane" : qUnion([Q0])});
            skCircle(sketch, "E111.0", {"center": v(23.25, 4.85) * mm, "radius": 4.65 * mm});
            skCircle(sketch, "E112.0", {"center": v(23.25, 4.85) * mm, "radius": 3.75 * mm});
            skSolve(sketch);
        }
        {
            var Q0;
            Q0 = qSketchRegion(id + "F21", true);
            extrude(context, id + "F22", {"entities" : qUnion([Q0]), "depth" : 18.5 * mm});
        }
        {
            var Q0;
            Q0=makeQuery(id+"F22.opExtrude","SWEPT_BODY",BODY,{"disambiguationData":[OSD([sQuery(id+"F21.wireOp",EDGE,"E111.0"),sQuery(id+"F21.wireOp",EDGE,"E112.0")])]});
            var Q1;
            Q1=makeQuery(id+"F16.opExtrude","SWEPT_BODY",BODY,{"disambiguationData":[OSD([sQuery(id+"F15.wireOp",EDGE,"E103.0"),sQuery(id+"F15.wireOp",EDGE,"E103.1"),sQuery(id+"F15.wireOp",EDGE,"E103.2"),sQuery(id+"F15.wireOp",EDGE,"E103.3")])]});
            var Q2;
            Q2=makeQuery(id+"F1.opExtrude","SWEPT_BODY",BODY,{"disambiguationData":[OSD([sQuery(id+"F0.wireOp",EDGE,"E0"),sQuery(id+"F0.wireOp",EDGE,"E1"),sQuery(id+"F0.wireOp",EDGE,"E3.MirrorCS"),sQuery(id+"F0.wireOp",EDGE,"E4.MirrorCS"),sQuery(id+"F0.wireOp",EDGE,"E5.MirrorCS"),sQuery(id+"F0.wireOp",EDGE,"E6.MirrorCS"),sQuery(id+"F0.wireOp",EDGE,"E7.MirrorCS"),sQuery(id+"F0.wireOp",EDGE,"E8.MirrorCS"),sQuery(id+"F0.wireOp",EDGE,"E9.MirrorCS"),sQuery(id+"F0.wireOp",EDGE,"E10.MirrorCS"),sQuery(id+"F0.wireOp",EDGE,"E11.MirrorCS"),sQuery(id+"F0.wireOp",EDGE,"E12.bottom"),sQuery(id+"F0.wireOp",EDGE,"E12.top"),sQuery(id+"F0.wireOp",EDGE,"E12.left"),sQuery(id+"F0.wireOp",EDGE,"E12.right")])]});
            booleanBodies(context, id + "F23", {"operationType" : BooleanOperationType.UNION, "tools" : qUnion([Q0, Q1, Q2])});
        }
        {
            var Q0;
            Q0=makeQuery(id+"F1.opExtrude","SWEPT_EDGE",EDGE,{"disambiguationData":[OSD([sQuery(id+"F0.wireOp",EDGE,"E9.MirrorCS"),sQuery(id+"F0.wireOp",EDGE,"E11.MirrorCS")])]});
            fillet(context, id + "F24", {"entities" : qUnion([Q0]), "radius" : 5 * mm, "tangentPropagation" : true, "allowEdgeOverflow" : false});
        }
        {
            var Q0;
            Q0=makeQuery(id+"F16.opExtrude","CAP_EDGE",EDGE,{"disambiguationData":[OSD([sQuery(id+"F15.wireOp",EDGE,"E103.1")])],"isStart":false});
            var Q1;
            Q1=makeQuery(id+"F16.opExtrude","CAP_EDGE",EDGE,{"disambiguationData":[OSD([sQuery(id+"F15.wireOp",EDGE,"E103.3")])],"isStart":false});
            fillet(context, id + "F25", {"entities" : qUnion([Q0, Q1]), "radius" : 5 * mm, "tangentPropagation" : true, "allowEdgeOverflow" : false});
        }
        {
            var Q0;
            Q0=makeQuery(id+"F7.boolean.opBoolean","COPY",EDGE,{"derivedFrom":makeQuery(id+"F7.opExtrude","CAP_EDGE",EDGE,{"disambiguationData":[OSD([sQuery(id+"F6.wireOp",EDGE,"E73.1")])],"isStart":true})});
            var Q1;
            {var subQ0=sQuery(id+"F15.wireOp",EDGE,"E103.3");var subQ2=sQuery(id+"F15.wireOp",EDGE,"E103.1");var subQ3=sQuery(id+"F15.wireOp",EDGE,"E103.0");var subQ6=makeQuery(id+"F16.opExtrude","SWEPT_FACE",FACE,{"disambiguationData":[OSD([subQ3])]});Q1=makeQuery(id+"F23.opBoolean","MERGE",FACE,{"derivedFrom":[makeQuery(id+"F11.opExtrude","CAP_FACE",FACE,{"disambiguationData":[OSD([sQuery(id+"F0.wireOp",EDGE,"E33.1"),sQuery(id+"F0.wireOp",EDGE,"E33.2"),sQuery(id+"F0.wireOp",EDGE,"E33.3"),sQuery(id+"F9.wireOp",EDGE,"E91"),sQuery(id+"F9.wireOp",EDGE,"E92"),sQuery(id+"F9.wireOp",EDGE,"E95.1"),sQuery(id+"F9.wireOp",EDGE,"E95.2"),sQuery(id+"F9.wireOp",EDGE,"E95.3"),sQuery(id+"F9.wireOp",EDGE,"E98"),sQuery(id+"F9.wireOp",EDGE,"E99")])],"isStart":false}),makeQuery(id+"F20.boolean.opBoolean","SPLIT",FACE,{"disambiguationData":[TD([makeQuery(id+"F16.opExtrude","SWEPT_FACE",FACE,{"disambiguationData":[OSD([subQ2])]})])],"derivedFrom":subQ6}),makeQuery(id+"F20.boolean.opBoolean","SPLIT",FACE,{"disambiguationData":[TD([makeQuery(id+"F16.opExtrude","SWEPT_FACE",FACE,{"disambiguationData":[OSD([subQ0])]})])],"derivedFrom":subQ6})]});}
            var Q2;
            {var subQ0=sQuery(id+"F0.wireOp",EDGE,"E12.right");var subQ1=sQuery(id+"F0.wireOp",EDGE,"E12.left");var subQ2=sQuery(id+"F0.wireOp",EDGE,"E12.top");var subQ3=sQuery(id+"F0.wireOp",EDGE,"E12.bottom");Q2=makeQuery(id+"F23.opBoolean","MERGE",FACE,{"derivedFrom":[makeQuery(id+"F8.boolean.opBoolean","MERGE",FACE,{"derivedFrom":[makeQuery(id+"F1.opExtrude","CAP_FACE",FACE,{"disambiguationData":[OSD([sQuery(id+"F0.wireOp",EDGE,"E0"),sQuery(id+"F0.wireOp",EDGE,"E1"),sQuery(id+"F0.wireOp",EDGE,"E3.MirrorCS"),sQuery(id+"F0.wireOp",EDGE,"E4.MirrorCS"),sQuery(id+"F0.wireOp",EDGE,"E5.MirrorCS"),sQuery(id+"F0.wireOp",EDGE,"E6.MirrorCS"),sQuery(id+"F0.wireOp",EDGE,"E7.MirrorCS"),sQuery(id+"F0.wireOp",EDGE,"E8.MirrorCS"),sQuery(id+"F0.wireOp",EDGE,"E9.MirrorCS"),sQuery(id+"F0.wireOp",EDGE,"E10.MirrorCS"),sQuery(id+"F0.wireOp",EDGE,"E11.MirrorCS"),subQ3,subQ2,subQ1,subQ0])],"isStart":true}),makeQuery(id+"F8.opExtrude","CAP_FACE",FACE,{"disambiguationData":[OSD([subQ3,subQ2,subQ1,subQ0,sQuery(id+"F0.wireOp",EDGE,"E33.0"),sQuery(id+"F0.wireOp",EDGE,"E33.1"),sQuery(id+"F0.wireOp",EDGE,"E33.2"),sQuery(id+"F0.wireOp",EDGE,"E33.3")])],"isStart":true})]}),makeQuery(id+"F16.opExtrude","SWEPT_FACE",FACE,{"disambiguationData":[OSD([sQuery(id+"F15.wireOp",EDGE,"E103.2")])]})]});}
            var Q3;
            Q3=makeQuery(id+"F22.opExtrude","CAP_FACE",FACE,{"disambiguationData":[OSD([sQuery(id+"F21.wireOp",EDGE,"E111.0"),sQuery(id+"F21.wireOp",EDGE,"E112.0")])],"isStart":false});
            var Q4;
            Q4=makeQuery(id+"F7.boolean.opBoolean","COPY",EDGE,{"derivedFrom":makeQuery(id+"F7.opExtrude","CAP_EDGE",EDGE,{"disambiguationData":[OSD([sQuery(id+"F6.wireOp",EDGE,"E73.3")])],"isStart":true})});
            var Q5;
            Q5=makeQuery(id+"F13.boolean.opBoolean","COPY",EDGE,{"derivedFrom":makeQuery(id+"F13.opExtrude","CAP_EDGE",EDGE,{"disambiguationData":[OSD([sQuery(id+"F12.wireOp",EDGE,"E102")])],"isStart":true})});
            var Q6;
            Q6=makeQuery(id+"F13.boolean.opBoolean","INTERSECT",EDGE,{"derivedFrom":[makeQuery(id+"F8.opExtrude","SWEPT_FACE",FACE,{"disambiguationData":[OSD([sQuery(id+"F0.wireOp",EDGE,"E12.bottom")])]}),makeQuery(id+"F13.opExtrude","SWEPT_FACE",FACE,{"disambiguationData":[OSD([sQuery(id+"F12.wireOp",EDGE,"E102")])]})]});
            chamfer(context, id + "F26", {"entities" : qUnion([Q0, Q1, Q2, Q3, Q4, Q5, Q6]), "width" : .2 * mm, "tangentPropagation" : true});
        }
    });
